# Revit family: HerzCon-Direktanschluss für FanCoils 65mm LF,MF
name_source: partatom
category: Rohrzubehör
units: mm (PartAtom-declared; Revit-internal decimal feet)

## family parameters
Arbeitsebenenbasiert = Nein
Beim Laden mit Abzugskörper schneiden = Nein
Bemaßung runder Anschluss = Durchmesser verwenden
Gemeinsam genutzt = Nein
Immer vertikal = Ja
OmniClass-Nummer = 23.65.55.14
OmniClass-Titel = Valves for Liquid Services
Teiletyp = Unterbricht

## types (2) — shared parameters
Anwendungen = Die HerzCON wurden entwickelt, um eine einfache Verbindung zu Gebläsekonvektoren oder anderen Anschlusseinheiten herzustellen.
Ein HerzCON ist eine Einheit, bestehend aus einem druckunabhängigen Kombiventil-Volumenstromregler (4006), Herz-Schmutzfänger, Herz-Entleerungshahn (2512) und zwei Herz-Multifunktionskugelhähnen.
Das Ein-/ Aus Schalten sowie Modulieren ist über einen 0-10 V Stellantrieb möglich und kann bei Bedarf in eine GLT integriert werden.
Die Einheit optimiert die Energieeffizienz des Systems, da es eine druckunabhängige Regelung ist, die den vollen Regelbereich unabhängig von Druckschwankungen gewährleistet, während gleichzeitig ein konstanter Durchfluss sichergestellt wird.
Mit der HerzCON können auch Spül- und Absperrvorgänge durchgeführt werden.
Eine Einheit kann für Heizen und Kühlen verwendet werden.
Es gibt daher keinen Produktunterschied zwischen Heizen und Kühlen.
Der am Sieb angebrachte Ablasshahn ermöglicht ein Spülen, ohne dass der Siebkorb entfernt werden muss.
Außerdem kann der Siebkorb vor Ort gereinigt werden.
D01 = 13 mm
D02 = 16.5 mm  [stored 0.0541339 ft]
D03 = 14.5 mm  [stored 0.0475722 ft]
D04 = 10 mm  [stored 0.0328084 ft]
D05 = 16.75 mm  [stored 0.0549541 ft]
D06 = 20.5 mm  [stored 0.0672572 ft]
D07 = 7.5 mm  [stored 0.0246063 ft]
D10 = 13.5 mm  [stored 0.0442913 ft]
D11 = 10.75 mm  [stored 0.035269 ft]
D12 = 12 mm  [stored 0.0393701 ft]
Gehäuse = entzinkungsbeständiges Messing
H01 = 19.5 mm  [stored 0.0639764 ft]
H02 = 26.55 mm  [stored 0.0871063 ft]
H03 = 26 mm
H04 = 2.5 mm  [stored 0.0082021 ft]
H05 = 18.5 mm  [stored 0.0606955 ft]
H06 = 8 mm  [stored 0.0262467 ft]
H07 = 27.8 mm  [stored 0.0912073 ft]
H08 = 2 mm  [stored 0.00656168 ft]
H09 = 7.2 mm  [stored 0.023622 ft]
H10 = 2 mm  [stored 0.00656168 ft]
H11 = 58.8 mm  [stored 0.192913 ft]
H15 = 75 mm
H16 = 34 mm
Hersteller = HERZ Armaturen Ges.m.b.H.
Hub = 4 mm
ISO01 = 181 mm
ISO02 = 176 mm
ISO03 = 15 mm  [stored 0.0492126 ft]
ISO04 = 47 mm  [stored 0.154199 ft]
ISO05 = 49 mm  [stored 0.160761 ft]
ISO06 = 114 mm  [stored 0.374016 ft]
ISO07 = -47 mm  [stored -0.154199 ft]
ISO08 = 134 mm
ISOH01 = 50 mm  [stored 0.164042 ft]
ISOH02 = -38 mm  [stored -0.124672 ft]
ISOR01 = 17.5 mm  [stored 0.0574147 ft]
Isolierschalen = EPP, wasserdampfdiffusionsdicht, schwarz
KombiH04 = 23.6 mm  [stored 0.0774278 ft]
L01 = 6 mm  [stored 0.019685 ft]
L02 = 5 mm  [stored 0.0164042 ft]
L03 = 7 mm  [stored 0.0229659 ft]
Max. Betriebsdruck = 2500000.0 Pa
Max. Betriebstemperatur = 130 °C
Medium = Heizungswasser gemäß ÖNORM H5195 oder VDI-Standard 2035.
Die Verwendung von Ethylen- oder Propylenglykol-Gemischen in einem Verhältnis von 25-50 Vol.- % ist erlaubt.
Membrane und O-Ringe = EPDM
Min. Betriebstemperatur = -20 °C
SCRNCODE = 05;04;04
SCRNSEQ = ARM;TYP_ARM="DURR";02
SFD02 = 18 mm  [stored 0.0590551 ft]
SFD03 = 13.5 mm  [stored 0.0442913 ft]
SFH03 = 32.5 mm  [stored 0.106627 ft]
SFH04 = 26 mm
SFH05 = 19.5 mm  [stored 0.0639764 ft]
SFL01 = 17 mm  [stored 0.0557743 ft]
SFL02 = 12.4 mm
SFR01 = 16.5 mm  [stored 0.0541339 ft]
SFR02 = 5.5 mm  [stored 0.0180446 ft]
URL = www.herz-armaturen.at
WI00 = 45.00°
WI01 = 120.00°
zero-valued in all types: Vorgabe-Ansicht

## type names (no varying parameters)
- DN15 LF
- DN15 MF

note: [stored X ft] marks values corroborated as IEEE doubles in the binary element streams (Revit-internal decimal feet)
